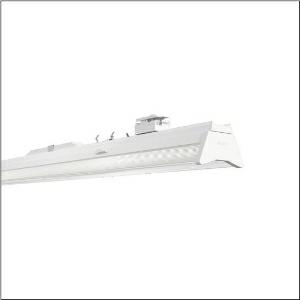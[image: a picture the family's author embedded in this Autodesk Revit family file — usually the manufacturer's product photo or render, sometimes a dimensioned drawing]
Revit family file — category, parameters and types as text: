
# Revit family: licross_r__21_performance_mo_52td16dn66xg_64f4
name_source: partatom
category: Lighting Fixtures
units: mm (PartAtom-declared; Revit-internal decimal feet)

## family parameters
Cut with Voids When Loaded = No
Host = Face
Light Source = No
Part Type = Normal
Room Calculation Point = No
Round Connector Dimension = Use Diameter
Shared = No

## types (1)
- --- (1 x LED, 6000 lm, 33.8 W, 6500K)
    Apparent Load = 34 VA
    CIE Flux Codes = 66 88 96 79 100
    Color Rendering = 80
    Color Temperature = 6500K
    Default Elevation = 1800 mm
    Description = Licross® 21 Performance MO, luminaire insert, of sheet steel, galvanised, coil coated, white, length: 1.500mm, width: 120mm, height: 123mm, LED rated luminous flux: 6.000lm, light colour: 865, control gear: DALI 2, with plug, 5-pole, with phase selection, mains connection: 220..240V, AC, 50/60Hz, rated input power: 34W, halogen-free wiring, primary light control with lens, of plastic, primary optical cover: cover, of PMMA, light emission: direct/indirect distribution, primary light characteristic: symmetric, protection rating (complete): IP54, insulation class (complete): insulation class I (protective earthing), certification: CE, ENEC, VDE, UKCA, protection symbol: D if used in an environment with non-conductive dust loads with corresponding accessories, impact resistance: IK06, permissible ambient temperature for indoor applications: -25..+45°C, corresponds to IFS (International Featured Standards) requirements for safety and quality in the food industry, reducing of maximum allowable ambient temperature of 5°C with ceiling mounting, LABS conformity tested according to VDMA 24364:2018-05, packaging unit: 1 piece
    Height = 114 mm
    Lamp = 1 x LED
    Lamp Light Flux = 6000 lm
    Lamp Power = 33.8 W
    Lamp count = 1
    Length = 1500 mm
    Luminous efficacy = 178 lm/W
    Manufacturer = Siteco
    ModVariant = No
    Model = 52TD16DN66XG
    Mounting Place = Ceiling
    Mounting Type = Pendant
    Number of Poles = 1
    OnlyDefault = Yes
    Power Factor = 1
    Product Name = Licross® 21 Performance MO
    Product group = luminaire insert
    ProductGroupID = 902
    Protection Class = Protection class I
    Protection Degree = IP 54
    RLX_Detail_Level = 1
    RLX_Emergency_Light_Flux = 0 lm
    RLX_Emergency_Type = 0
    RLX_Emergency_Type_DB = No
    RlxData = <blob elided: 33641 chars, md5=6d0f68e5>
    Socket = socket
    Standby Power = 0 W
    System Light Flux = 6000 lm
    System Power = 34 W
    Type Comments = factory setting: luminous flux: 100 % | dim-lin: 254 | 229 mA
    Type Image = l_1256138.jpg
    URL = http://relux.com
    VarID = @adj_022744
    Voltage = 0 V
    Weight = 0.00 kg
    Width = 120 mm

## geometry (parser evidence)
native form markers: Blend x4, Sweep x12
no freeform markers — native parametric forms only
